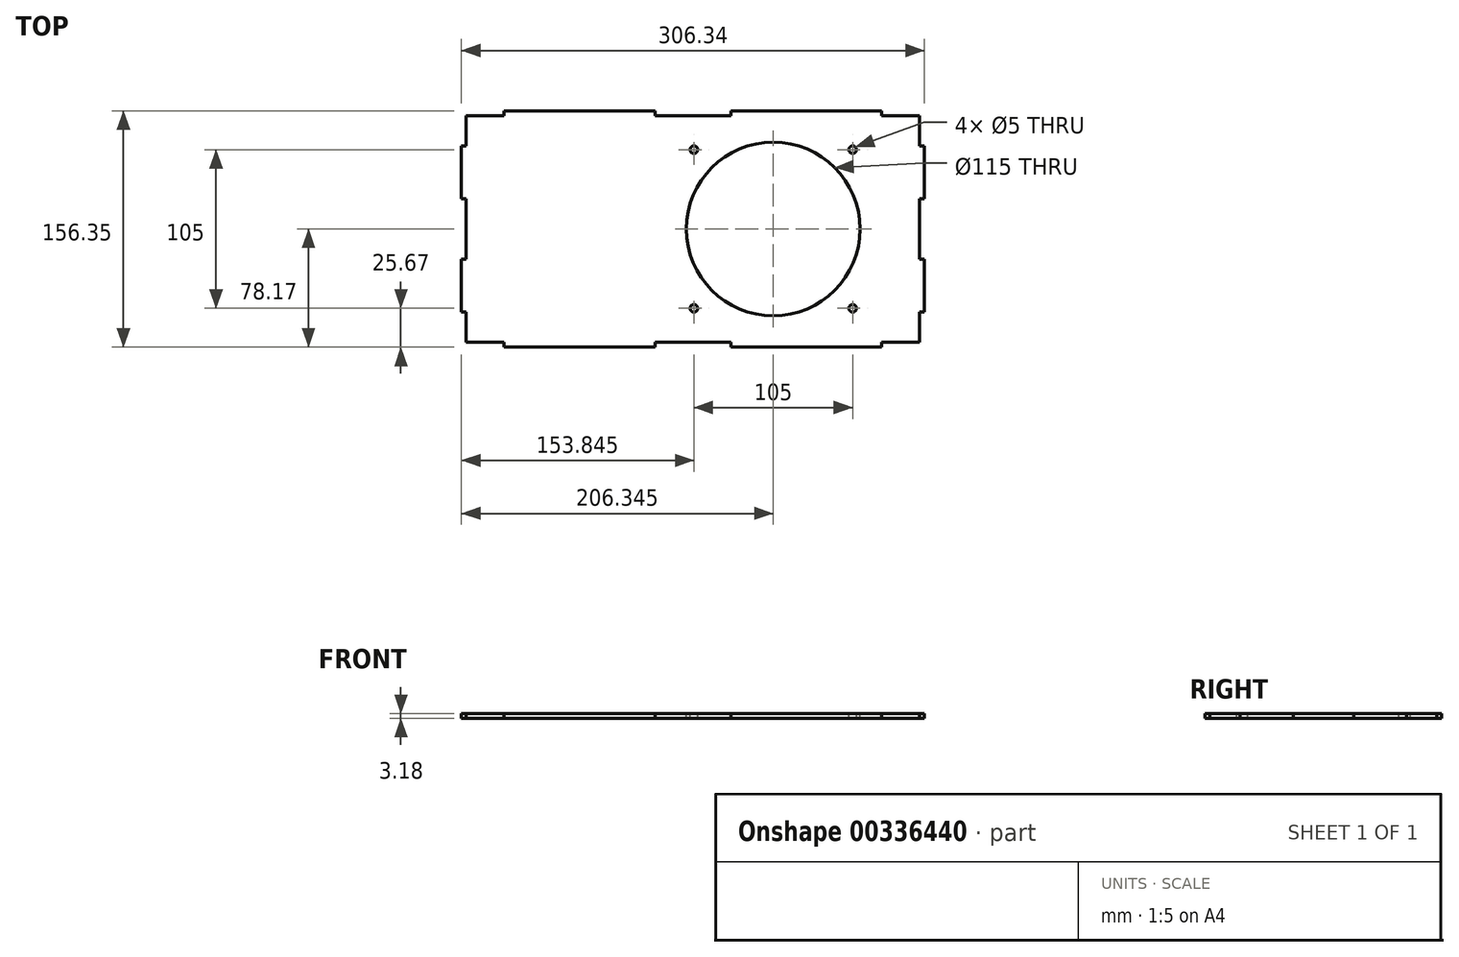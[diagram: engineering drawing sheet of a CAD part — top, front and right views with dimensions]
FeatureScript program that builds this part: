
annotation { "Feature Type Name" : "Feature", "Feature Type Description" : "" }
export const myFeature = defineFeature(function(context is Context, id is Id, definition is map)
    precondition{}
    {
        {
            var Q0;
            Q0=qCreatedBy(makeId("Top.planeOp"),FACE);
            var sketch = newSketch(context, id + "F0", { "sketchPlane" : qUnion([Q0])});
            skLineSegment(sketch, "E0", {"start": v(0, 0) * mm, "end": v(0, 150) * mm, "construction": true});
            skLineSegment(sketch, "E1", {"start": v(0, 150) * mm, "end": v(300, 150) * mm, "construction": true});
            skLineSegment(sketch, "E2", {"start": v(300, 150) * mm, "end": v(300, 0) * mm, "construction": true});
            skLineSegment(sketch, "E3", {"start": v(300, 0) * mm, "end": v(0, 0) * mm, "construction": true});
            skLineSegment(sketch, "E4", {"start": v(150, 150) * mm, "end": v(150, 0) * mm, "construction": true});
            skLineSegment(sketch, "E5", {"start": v(150, 0) * mm, "end": v(125, 0) * mm});
            skLineSegment(sketch, "E6", {"start": v(125, 0) * mm, "end": v(125, -3.18) * mm});
            skLineSegment(sketch, "E7", {"start": v(125, -3.18) * mm, "end": v(25, -3.18) * mm});
            skLineSegment(sketch, "E8", {"start": v(25, -3.18) * mm, "end": v(25, 0) * mm});
            skLineSegment(sketch, "E9", {"start": v(25, 0) * mm, "end": v(0, 0) * mm});
            skLineSegment(sketch, "E10", {"start": v(0, 20) * mm, "end": v(-3.18, 20) * mm});
            skLineSegment(sketch, "E11", {"start": v(-3.18, 20) * mm, "end": v(-3.18, 55) * mm});
            skLineSegment(sketch, "E12", {"start": v(-3.18, 55) * mm, "end": v(0, 55) * mm});
            skLineSegment(sketch, "E13", {"start": v(0, 75) * mm, "end": v(150, 75) * mm, "construction": true});
            skLineSegment(sketch, "E14.MirrorCS", {"start": v(0, 130) * mm, "end": v(-3.18, 130) * mm});
            skLineSegment(sketch, "E15.MirrorCS", {"start": v(-3.18, 95) * mm, "end": v(0, 95) * mm});
            skLineSegment(sketch, "E16.MirrorCS", {"start": v(125, 150) * mm, "end": v(125, 153.18) * mm});
            skLineSegment(sketch, "E17.MirrorCS", {"start": v(25, 153.18) * mm, "end": v(25, 150) * mm});
            skLineSegment(sketch, "E18.MirrorCS", {"start": v(25, 150) * mm, "end": v(0, 150) * mm});
            skLineSegment(sketch, "E19.MirrorCS", {"start": v(125, 153.18) * mm, "end": v(25, 153.18) * mm});
            skLineSegment(sketch, "E20.MirrorCS", {"start": v(-3.18, 130) * mm, "end": v(-3.18, 95) * mm});
            skLineSegment(sketch, "E21.MirrorCS", {"start": v(150, 150) * mm, "end": v(125, 150) * mm});
            skLineSegment(sketch, "E22", {"start": v(0, 95) * mm, "end": v(0, 55) * mm});
            skLineSegment(sketch, "E23", {"start": v(0, 150) * mm, "end": v(0, 130) * mm});
            skLineSegment(sketch, "E24", {"start": v(0, 20) * mm, "end": v(0, 0) * mm});
            skLineSegment(sketch, "E25.MirrorCS", {"start": v(175, 150) * mm, "end": v(175, 153.18) * mm});
            skLineSegment(sketch, "E26.MirrorCS", {"start": v(175, 0) * mm, "end": v(175, -3.18) * mm});
            skLineSegment(sketch, "E27.MirrorCS", {"start": v(275, -3.18) * mm, "end": v(275, 0) * mm});
            skLineSegment(sketch, "E28.MirrorCS", {"start": v(300, 20) * mm, "end": v(303.18, 20) * mm});
            skLineSegment(sketch, "E29.MirrorCS", {"start": v(275, 153.18) * mm, "end": v(275, 150) * mm});
            skLineSegment(sketch, "E30.MirrorCS", {"start": v(303.18, 55) * mm, "end": v(300, 55) * mm});
            skLineSegment(sketch, "E31.MirrorCS", {"start": v(303.18, 95) * mm, "end": v(300, 95) * mm});
            skLineSegment(sketch, "E32.MirrorCS", {"start": v(300, 130) * mm, "end": v(303.18, 130) * mm});
            skLineSegment(sketch, "E33.MirrorCS", {"start": v(275, 0) * mm, "end": v(300, 0) * mm});
            skLineSegment(sketch, "E34.MirrorCS", {"start": v(300, 20) * mm, "end": v(300, 0) * mm});
            skLineSegment(sketch, "E35.MirrorCS", {"start": v(175, -3.18) * mm, "end": v(275, -3.18) * mm});
            skLineSegment(sketch, "E36.MirrorCS", {"start": v(303.18, 20) * mm, "end": v(303.18, 55) * mm});
            skLineSegment(sketch, "E37.MirrorCS", {"start": v(150, 150) * mm, "end": v(175, 150) * mm});
            skLineSegment(sketch, "E38.MirrorCS", {"start": v(150, 0) * mm, "end": v(175, 0) * mm});
            skLineSegment(sketch, "E39.MirrorCS", {"start": v(175, 153.18) * mm, "end": v(275, 153.18) * mm});
            skLineSegment(sketch, "E40.MirrorCS", {"start": v(0, 0) * mm, "end": v(300, 0) * mm, "construction": true});
            skLineSegment(sketch, "E41.MirrorCS", {"start": v(300, 95) * mm, "end": v(300, 55) * mm});
            skLineSegment(sketch, "E42.MirrorCS", {"start": v(300, 75) * mm, "end": v(150, 75) * mm, "construction": true});
            skLineSegment(sketch, "E43.MirrorCS", {"start": v(300, 150) * mm, "end": v(0, 150) * mm, "construction": true});
            skLineSegment(sketch, "E44.MirrorCS", {"start": v(300, 150) * mm, "end": v(300, 130) * mm});
            skLineSegment(sketch, "E45.MirrorCS", {"start": v(275, 150) * mm, "end": v(300, 150) * mm});
            skLineSegment(sketch, "E46.MirrorCS", {"start": v(300, 0) * mm, "end": v(300, 150) * mm, "construction": true});
            skLineSegment(sketch, "E47.MirrorCS", {"start": v(303.18, 130) * mm, "end": v(303.18, 95) * mm});
            skSolve(sketch);
        }
        {
            var Q0;
            Q0=makeQuery(id+"F0.imprint","IMPRINT",FACE,{"disambiguationData":[TD([[makeQuery(id+"F0.imprint","IMPRINT",EDGE,{"derivedFrom":sQuery(id+"F0.wireOp",EDGE,"E5")}),-1.0]])]});
            extrude(context, id + "F1", {"entities" : qUnion([Q0]), "depth" : 3.17 * mm});
        }
        {
            var Q0;
            Q0=makeQuery(id+"F1.opExtrude","CAP_FACE",FACE,{"disambiguationData":[OSD([sQuery(id+"F0.wireOp",EDGE,"E5"),sQuery(id+"F0.wireOp",EDGE,"E6"),sQuery(id+"F0.wireOp",EDGE,"E7"),sQuery(id+"F0.wireOp",EDGE,"E8"),sQuery(id+"F0.wireOp",EDGE,"E9"),sQuery(id+"F0.wireOp",EDGE,"E10"),sQuery(id+"F0.wireOp",EDGE,"E11"),sQuery(id+"F0.wireOp",EDGE,"E12"),sQuery(id+"F0.wireOp",EDGE,"E14.MirrorCS"),sQuery(id+"F0.wireOp",EDGE,"E15.MirrorCS"),sQuery(id+"F0.wireOp",EDGE,"E16.MirrorCS"),sQuery(id+"F0.wireOp",EDGE,"E17.MirrorCS"),sQuery(id+"F0.wireOp",EDGE,"E18.MirrorCS"),sQuery(id+"F0.wireOp",EDGE,"E19.MirrorCS"),sQuery(id+"F0.wireOp",EDGE,"E20.MirrorCS"),sQuery(id+"F0.wireOp",EDGE,"E21.MirrorCS"),sQuery(id+"F0.wireOp",EDGE,"E22"),sQuery(id+"F0.wireOp",EDGE,"E23"),sQuery(id+"F0.wireOp",EDGE,"E24"),sQuery(id+"F0.wireOp",EDGE,"E25.MirrorCS"),sQuery(id+"F0.wireOp",EDGE,"E26.MirrorCS"),sQuery(id+"F0.wireOp",EDGE,"E27.MirrorCS"),sQuery(id+"F0.wireOp",EDGE,"E28.MirrorCS"),sQuery(id+"F0.wireOp",EDGE,"E29.MirrorCS"),sQuery(id+"F0.wireOp",EDGE,"E30.MirrorCS"),sQuery(id+"F0.wireOp",EDGE,"E31.MirrorCS"),sQuery(id+"F0.wireOp",EDGE,"E32.MirrorCS"),sQuery(id+"F0.wireOp",EDGE,"E33.MirrorCS"),sQuery(id+"F0.wireOp",EDGE,"E34.MirrorCS"),sQuery(id+"F0.wireOp",EDGE,"E35.MirrorCS"),sQuery(id+"F0.wireOp",EDGE,"E36.MirrorCS"),sQuery(id+"F0.wireOp",EDGE,"E37.MirrorCS"),sQuery(id+"F0.wireOp",EDGE,"E38.MirrorCS"),sQuery(id+"F0.wireOp",EDGE,"E39.MirrorCS"),sQuery(id+"F0.wireOp",EDGE,"E41.MirrorCS"),sQuery(id+"F0.wireOp",EDGE,"E44.MirrorCS"),sQuery(id+"F0.wireOp",EDGE,"E45.MirrorCS"),sQuery(id+"F0.wireOp",EDGE,"E47.MirrorCS")])],"isStart":false});
            var sketch = newSketch(context, id + "F2", { "sketchPlane" : qUnion([Q0])});
            skLineSegment(sketch, "E48", {"start": v(0, 75) * mm, "end": v(300, 75) * mm, "construction": true});
            skLineSegment(sketch, "E49", {"start": v(203.18, 153.18) * mm, "end": v(203.18, -3.18) * mm, "construction": true});
            skCircle(sketch, "E50", {"center": v(203.18, 75) * mm, "radius": 57.5 * mm});
            skCircle(sketch, "E51", {"center": v(150.67, 127.5) * mm, "radius": 2.5 * mm});
            skCircle(sketch, "E52.MirrorC", {"center": v(150.68, 22.5) * mm, "radius": 2.5 * mm});
            skCircle(sketch, "E53.MirrorC", {"center": v(255.68, 127.5) * mm, "radius": 2.5 * mm});
            skCircle(sketch, "E54.MirrorC", {"center": v(255.68, 22.5) * mm, "radius": 2.5 * mm});
            skSolve(sketch);
        }
        {
            var Q0;
            Q0 = qSketchRegion(id + "F2", true);
            extrude(context, id + "F3", {"entities" : qUnion([Q0]), "operationType" : NewBodyOperationType.REMOVE, "endBound" : BoundingType.THROUGH_ALL, "oppositeDirection" : true, "depth" : 25 * mm});
        }
    });
